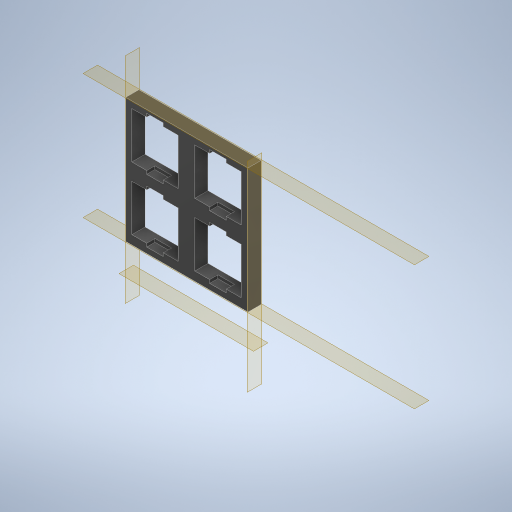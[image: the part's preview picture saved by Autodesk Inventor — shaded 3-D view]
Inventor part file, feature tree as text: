
AUTODESK INVENTOR PART (.ipt)
format: ipt  version: 2024 (Build 280153000, 153)  size: 736,256 bytes
history: native  units: mm
features: split x4, plane x3, other x2
ambient origin geometry x8: Origin, YZ Plane, XZ Plane, XY Plane, X Axis, Y Axis, Z Axis, Center Point
bodies: Solid1 (feature_tree)
feature tree (9):
  other  "8_button_macro_keypad_-_top_plate"
  other  "MeshFeature1"
  plane  "Work Plane1"
  plane  "Work Plane2"
  plane  "Work Plane3"
  split  "Split1"
  split  "Split2"
  split  "Split3"
  split  "Split4"
